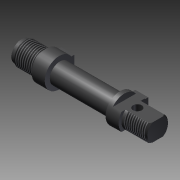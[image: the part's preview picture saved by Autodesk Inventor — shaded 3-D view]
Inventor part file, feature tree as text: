
AUTODESK INVENTOR PART (.ipt)
format: ipt  version: 2011 SP1 (Build 150282100, 282)  size: 179,712 bytes
history: native  units: mm
features: other x28, sketch x8, revolve x4, extrude x4, thread x2
ambient origin geometry x8: Origin, YZ Plane, XZ Plane, XY Plane, X Axis, Y Axis, Z Axis, Center Point
bodies: Solid1 (feature_tree)
feature tree (46):
  revolve  "Revolution1"  [1 undecoded]
  thread  "Thread1"  [1 undecoded]
  thread  "Thread2"  [1 undecoded]
  extrude  "Extrusion1"  TaperAngle=360.0deg  [1 undecoded]
  extrude  "Extrusion2"  Depth=24.0mm TaperAngle=0.0deg
  revolve  "Revolution2"  Angle=360.0deg
  extrude  "Extrusion3"  [1 undecoded]
  extrude  "Extrusion4"  [1 undecoded]
  revolve  "Revolution3"  [1 undecoded]
  revolve  "Revolution4"  [1 undecoded]
  other  "C1_XY"
  other  "C1_YZ"
  other  "C1_ZX"
  other  "C1_X"
  other  "C1_Y"
  other  "C1_Z"
  other  "C1_Center"
  other  "CD1_XY"
  other  "CD1_YZ"
  other  "CD1_ZX"
  other  "CD1_X"
  other  "CD1_Y"
  other  "CD1_Z"
  other  "CD1_Center"
  other  "CD2_XY"
  other  "CD2_YZ"
  other  "CD2_ZX"
  other  "CD2_X"
  other  "CD2_Y"
  other  "CD2_Z"
  other  "CD2_Center"
  other  "RL_XY"
  other  "RL_YZ"
  other  "RL_ZX"
  other  "RL_X"
  other  "RL_Y"
  other  "RL_Z"
  other  "RL_Center"
  sketch  "Skizze_1"  dims[d0=360.0deg d1=12.08mm d2=0.0mm d3=14.4865mm d4=0.0mm d5=9.0mm d6=0.0mm]
  sketch  "Skizze_3"  dims[d14=360.0deg d15=360.0deg]
  sketch  "Skizze_4"
  sketch  "Skizze_16_ALT_Drilling_1"  dims[d7=9.0mm d8=0.0mm d9=360.0deg]
  sketch  "Skizze_7"
  sketch  "Skizze_8"
  sketch  "Skizze_9_ALT_Drilling_2"  dims[d10=24.0mm d11=0.0mm d12=24.0mm d13=0.0mm]
  sketch  "Skizze_10_ALT_Drilling_3"  dims[d16=0.0mm d17=0.0mm d18=0.0mm d19=0.0mm]
note: 8 required parameter values undecoded (feature->parameter linkage not recoverable at this tier; creation-order binding heuristic only, values carry confidence <= 0.55)